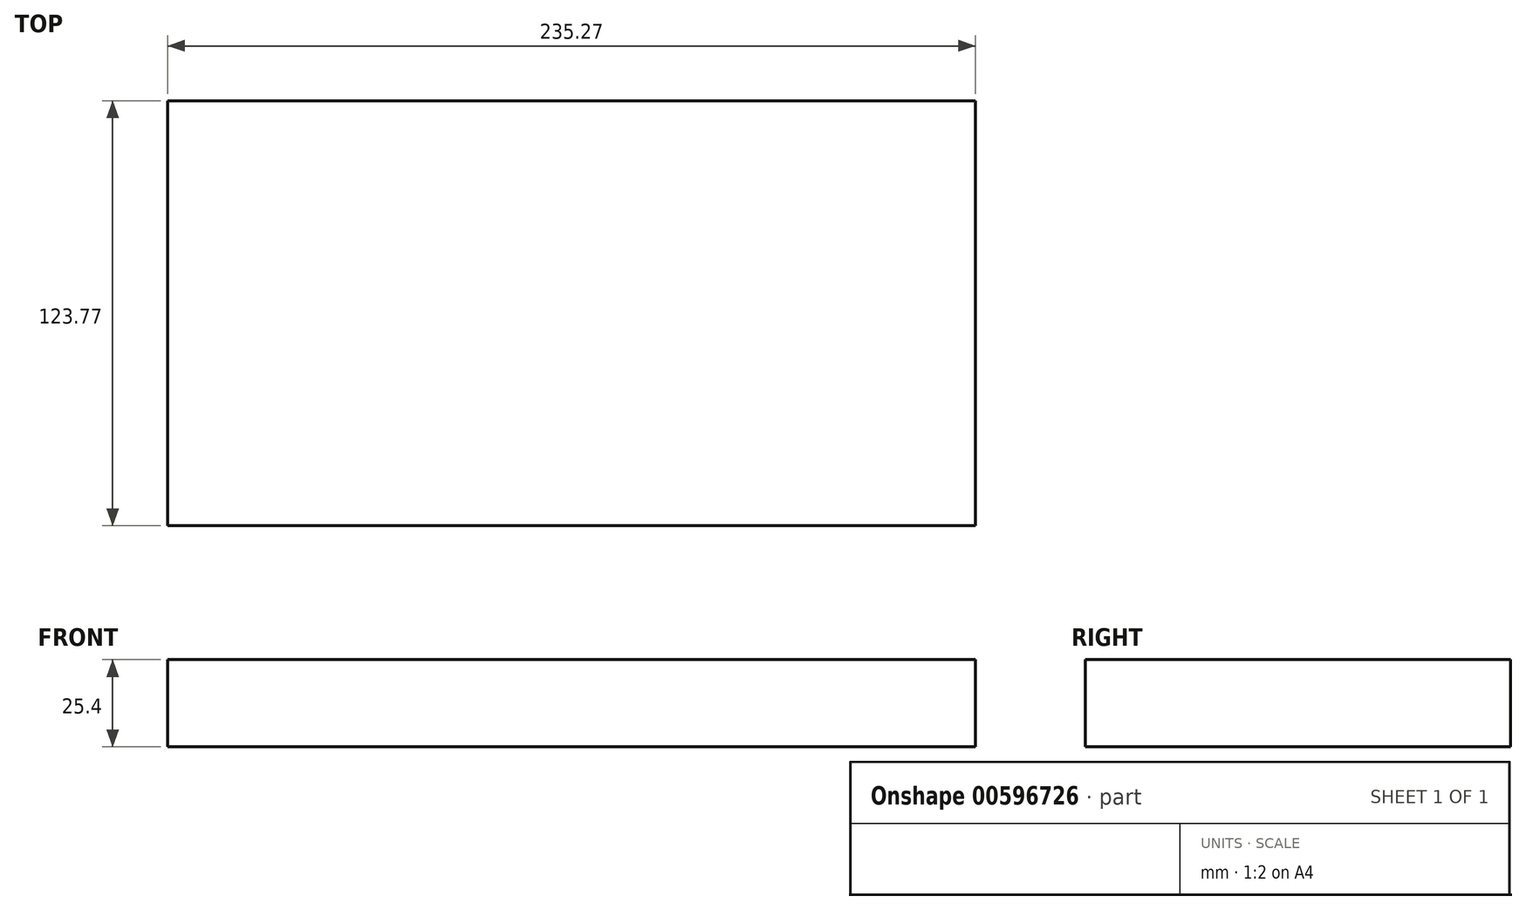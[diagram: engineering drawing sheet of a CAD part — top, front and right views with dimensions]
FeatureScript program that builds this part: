
annotation { "Feature Type Name" : "Feature", "Feature Type Description" : "" }
export const myFeature = defineFeature(function(context is Context, id is Id, definition is map)
    precondition{}
    {
        {
            var Q0;
            Q0=qCreatedBy(makeId("Top.planeOp"),FACE);
            var sketch = newSketch(context, id + "F0", { "sketchPlane" : qUnion([Q0])});
            skLineSegment(sketch, "E0.bottom", {"start": v(-120.35, 30.6) * mm, "end": v(114.92, 30.6) * mm});
            skLineSegment(sketch, "E0.top", {"start": v(-120.35, -93.16) * mm, "end": v(114.92, -93.16) * mm});
            skLineSegment(sketch, "E0.left", {"start": v(-120.35, 30.6) * mm, "end": v(-120.35, -93.16) * mm});
            skLineSegment(sketch, "E0.right", {"start": v(114.92, 30.6) * mm, "end": v(114.92, -93.16) * mm});
            skSolve(sketch);
        }
        {
            var Q0;
            Q0 = qSketchRegion(id + "F0", true);
            extrude(context, id + "F1", {"entities" : qUnion([Q0]), "depth" : 25.4 * mm, "offsetDistance" : 25.4 * mm});
        }
    });
